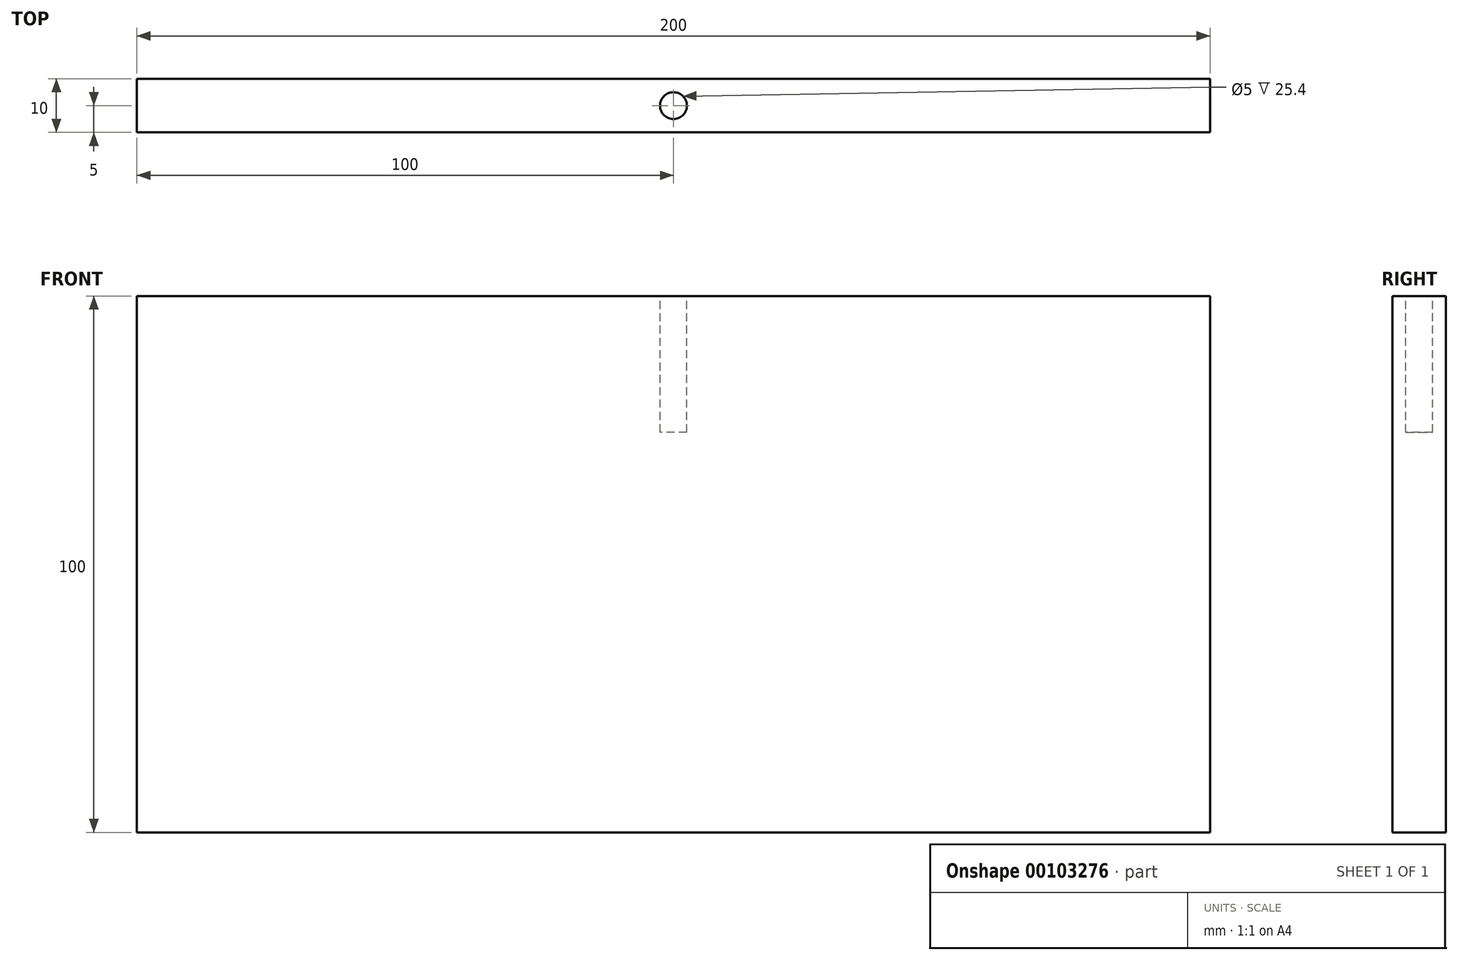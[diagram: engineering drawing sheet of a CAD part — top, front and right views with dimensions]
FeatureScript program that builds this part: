
annotation { "Feature Type Name" : "Feature", "Feature Type Description" : "" }
export const myFeature = defineFeature(function(context is Context, id is Id, definition is map)
    precondition{}
    {
        {
            var Q0;
            Q0=qCreatedBy(makeId("Front.planeOp"),FACE);
            var sketch = newSketch(context, id + "F0", { "sketchPlane" : qUnion([Q0])});
            skLineSegment(sketch, "E0.bottom", {"start": v(-100, 50) * mm, "end": v(100, 50) * mm});
            skLineSegment(sketch, "E0.top", {"start": v(-100, -50) * mm, "end": v(100, -50) * mm});
            skLineSegment(sketch, "E0.left", {"start": v(-100, 50) * mm, "end": v(-100, -50) * mm});
            skLineSegment(sketch, "E0.right", {"start": v(100, 50) * mm, "end": v(100, -50) * mm});
            skSolve(sketch);
        }
        {
            var Q0;
            Q0=makeQuery(id+"F0.imprint","IMPRINT",FACE,{"disambiguationData":[TD([[makeQuery(id+"F0.imprint","IMPRINT",EDGE,{"derivedFrom":sQuery(id+"F0.wireOp",EDGE,"E0.bottom")}),-1.0]])]});
            extrude(context, id + "F1", {"entities" : qUnion([Q0]), "endBound" : BoundingType.SYMMETRIC, "depth" : 10 * mm});
        }
        {
            var Q0;
            Q0=makeQuery(id+"F1.opExtrude","SWEPT_FACE",FACE,{"disambiguationData":[OSD([sQuery(id+"F0.wireOp",EDGE,"E0.bottom")])]});
            var sketch = newSketch(context, id + "F2", { "sketchPlane" : qUnion([Q0])});
            skCircle(sketch, "E1", {"center": v(0, 0) * mm, "radius": 2.5 * mm});
            skSolve(sketch);
        }
        {
            var Q0;
            Q0=makeQuery(id+"F2.imprint","IMPRINT",FACE,{"disambiguationData":[TD([[makeQuery(id+"F2.imprint","IMPRINT",EDGE,{"derivedFrom":sQuery(id+"F2.wireOp",EDGE,"E1")}),1.0]])]});
            extrude(context, id + "F3", {"entities" : qUnion([Q0]), "operationType" : NewBodyOperationType.REMOVE, "oppositeDirection" : true, "depth" : 25.4 * mm});
        }
    });
